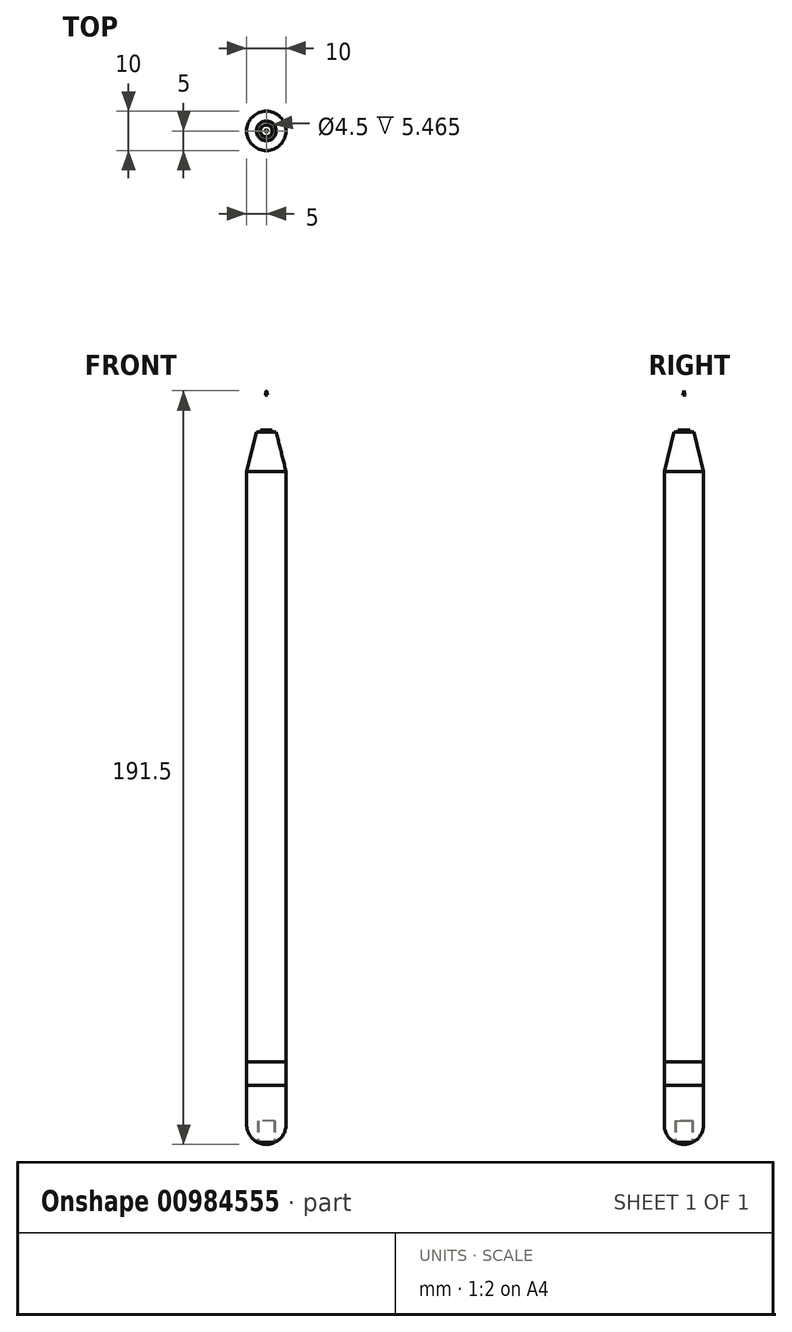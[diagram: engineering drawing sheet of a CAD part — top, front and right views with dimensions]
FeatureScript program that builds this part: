
annotation { "Feature Type Name" : "Feature", "Feature Type Description" : "" }
export const myFeature = defineFeature(function(context is Context, id is Id, definition is map)
    precondition{}
    {
        {
            var Q0;
            Q0=qCreatedBy(makeId("Top.planeOp"),FACE);
            var sketch = newSketch(context, id + "F0", { "sketchPlane" : qUnion([Q0])});
            skCircle(sketch, "E0", {"center": v(0, 0) * mm, "radius": 5 * mm});
            skSolve(sketch);
        }
        {
            var Q0;
            Q0=qSketchRegion(id+"F0",true);
            extrude(context, id + "F1", {"entities" : qUnion([Q0]), "endBound" : BoundingType.SYMMETRIC, "offsetDistance" : 25 * mm, "depth" : 150 * mm});
        }
        {
            var Q0;
            Q0=qCreatedBy(makeId("Front.planeOp"),FACE);
            var sketch = newSketch(context, id + "F2", { "sketchPlane" : qUnion([Q0])});
            skLineSegment(sketch, "E1", {"start": v(0, 85) * mm, "end": v(0, 75) * mm, "construction": true});
            skLineSegment(sketch, "E2.0", {"start": v(-5, 75) * mm, "end": v(5, 75) * mm, "construction": true});
            skLineSegment(sketch, "E3", {"start": v(-5, -75) * mm, "end": v(-5, 75) * mm, "construction": true});
            skLineSegment(sketch, "E4", {"start": v(5, 75) * mm, "end": v(5, -75) * mm, "construction": true});
            skLineSegment(sketch, "E5", {"start": v(-5, 75) * mm, "end": v(0, 75) * mm});
            skLineSegment(sketch, "E6", {"start": v(0, 85) * mm, "end": v(0, 75) * mm});
            skLineSegment(sketch, "E7", {"start": v(-5, 85) * mm, "end": v(-5, 75) * mm, "construction": true});
            skLineSegment(sketch, "E8", {"start": v(-5, 85) * mm, "end": v(0, 85) * mm, "construction": true});
            skLineSegment(sketch, "E9", {"start": v(-5, 75) * mm, "end": v(-2.5, 85) * mm});
            skLineSegment(sketch, "E10", {"start": v(-2.5, 85) * mm, "end": v(0, 85) * mm});
            skSolve(sketch);
        }
        {
            var Q0;
            Q0=qSketchRegion(id+"F2",true);
            var Q1;
            Q1=sQuery(id+"F2.wireOp",EDGE,"E1");
            revolve(context, id + "F3", {"operationType" : NewBodyOperationType.ADD, "entities" : qUnion([Q0]), "axis" : qUnion([Q1]), "revolveType" : RevolveType.FULL});
        }
        {
            var Q0;
            Q0=qCreatedBy(makeId("Front.planeOp"),FACE);
            var sketch = newSketch(context, id + "F4", { "sketchPlane" : qUnion([Q0])});
            skLineSegment(sketch, "E11", {"start": v(-2.5, 85.5) * mm, "end": v(0, 95.5) * mm});
            skLineSegment(sketch, "E12", {"start": v(0, 95.5) * mm, "end": v(0, 85.5) * mm});
            skLineSegment(sketch, "E13", {"start": v(-2.5, 85.5) * mm, "end": v(0, 85.5) * mm});
            skLineSegment(sketch, "E14", {"start": v(-1.5, 85.5) * mm, "end": v(-1.5, 85) * mm});
            skLineSegment(sketch, "E15", {"start": v(-1.5, 85) * mm, "end": v(0, 85) * mm});
            skLineSegment(sketch, "E16", {"start": v(0, 85) * mm, "end": v(0, 85.5) * mm});
            skArc(sketch, "E17", {"start": v(-0.3, 94.34) * mm, "mid": v(-0.18, 94.5) * mm, "end": v(0, 94.56) * mm});
            skSolve(sketch);
        }
        {
            var Q0;
            {var subQ2=sQuery(id+"F4.wireOp",EDGE,"E14");Q0=makeQuery(id+"F4.imprint","IMPRINT",FACE,{"disambiguationData":[TD([[makeQuery(id+"F4.imprint","IMPRINT",EDGE,{"derivedFrom":subQ2}),1.0]])]});}
            var Q1;
            {var subQ6=sQuery(id+"F4.wireOp",EDGE,"E17");Q1=makeQuery(id+"F4.imprint","IMPRINT",FACE,{"disambiguationData":[TD([[makeQuery(id+"F4.imprint","IMPRINT",EDGE,{"derivedFrom":subQ6}),-1.0]])]});}
            var Q2;
            Q2=sQuery(id+"F4.wireOp",EDGE,"E12");
            revolve(context, id + "F5", {"entities" : qUnion([Q0, Q1]), "axis" : qUnion([Q2]), "revolveType" : RevolveType.FULL});
        }
        {
            var Q0;
            Q0=qCreatedBy(makeId("Front.planeOp"),FACE);
            var sketch = newSketch(context, id + "F6", { "sketchPlane" : qUnion([Q0])});
            skLineSegment(sketch, "E18", {"start": v(0, -81) * mm, "end": v(0, -74.97) * mm});
            skLineSegment(sketch, "E19", {"start": v(0, -81) * mm, "end": v(5, -81) * mm});
            skLineSegment(sketch, "E20", {"start": v(5, -81) * mm, "end": v(5, -75) * mm});
            skLineSegment(sketch, "E21.0", {"start": v(-5, -75) * mm, "end": v(5, -75) * mm});
            skSolve(sketch);
        }
        {
            var Q0;
            Q0=qSketchRegion(id+"F6",true);
            var Q1;
            Q1=sQuery(id+"F6.wireOp",EDGE,"E18");
            revolve(context, id + "F7", {"entities" : qUnion([Q0]), "axis" : qUnion([Q1]), "revolveType" : RevolveType.FULL});
        }
        {
            var Q0;
            Q0=qCreatedBy(makeId("Front.planeOp"),FACE);
            var sketch = newSketch(context, id + "F8", { "sketchPlane" : qUnion([Q0])});
            skLineSegment(sketch, "E22.bottom", {"start": v(0, -96) * mm, "end": v(-5, -96) * mm});
            skLineSegment(sketch, "E22.top", {"start": v(0, -81) * mm, "end": v(-5, -81) * mm});
            skLineSegment(sketch, "E22.left", {"start": v(0, -96) * mm, "end": v(0, -81) * mm});
            skLineSegment(sketch, "E22.right", {"start": v(-5, -96) * mm, "end": v(-5, -81) * mm});
            skLineSegment(sketch, "E23.0", {"start": v(5, -81) * mm, "end": v(-5, -81) * mm, "construction": true});
            skArc(sketch, "E24", {"start": v(0, -96) * mm, "mid": v(-3.54, -94.54) * mm, "end": v(-5, -91) * mm});
            skSolve(sketch);
        }
        {
            var Q0;
            {var subQ0=sQuery(id+"F8.wireOp",EDGE,"E22.top");Q0=makeQuery(id+"F8.imprint","IMPRINT",FACE,{"disambiguationData":[TD([[makeQuery(id+"F8.imprint","IMPRINT",EDGE,{"derivedFrom":subQ0}),1.0]])]});}
            var Q1;
            Q1=sQuery(id+"F8.wireOp",EDGE,"E22.left");
            revolve(context, id + "F9", {"entities" : qUnion([Q0]), "axis" : qUnion([Q1]), "revolveType" : RevolveType.FULL});
        }
        {
            var Q0;
            Q0=qCreatedBy(makeId("Top.planeOp"),FACE);
            cPlane(context, id + "F10", {"entities" : qUnion([Q0]), "cplaneType" : CPlaneType.OFFSET, "offset" : 95 * mm, "oppositeDirection" : true, "width" : 150 * mm, "height" : 150 * mm});
        }
        {
            var Q0;
            Q0=qCreatedBy(id+"F10.planeOp",FACE);
            var sketch = newSketch(context, id + "F11", { "sketchPlane" : qUnion([Q0])});
            skCircle(sketch, "E25", {"center": v(0, 0) * mm, "radius": 2.25 * mm});
            skCircle(sketch, "E26", {"center": v(0, 0) * mm, "radius": 2 * mm});
            skSolve(sketch);
        }
        {
            var Q0;
            Q0=qSketchRegion(id+"F11",true);
            extrude(context, id + "F12", {"entities" : qUnion([Q0]), "operationType" : NewBodyOperationType.REMOVE, "depth" : 5 * mm, "hasSecondDirection" : true, "secondDirectionOppositeDirection" : true, "secondDirectionDepth" : 25 * mm});
        }
    });
